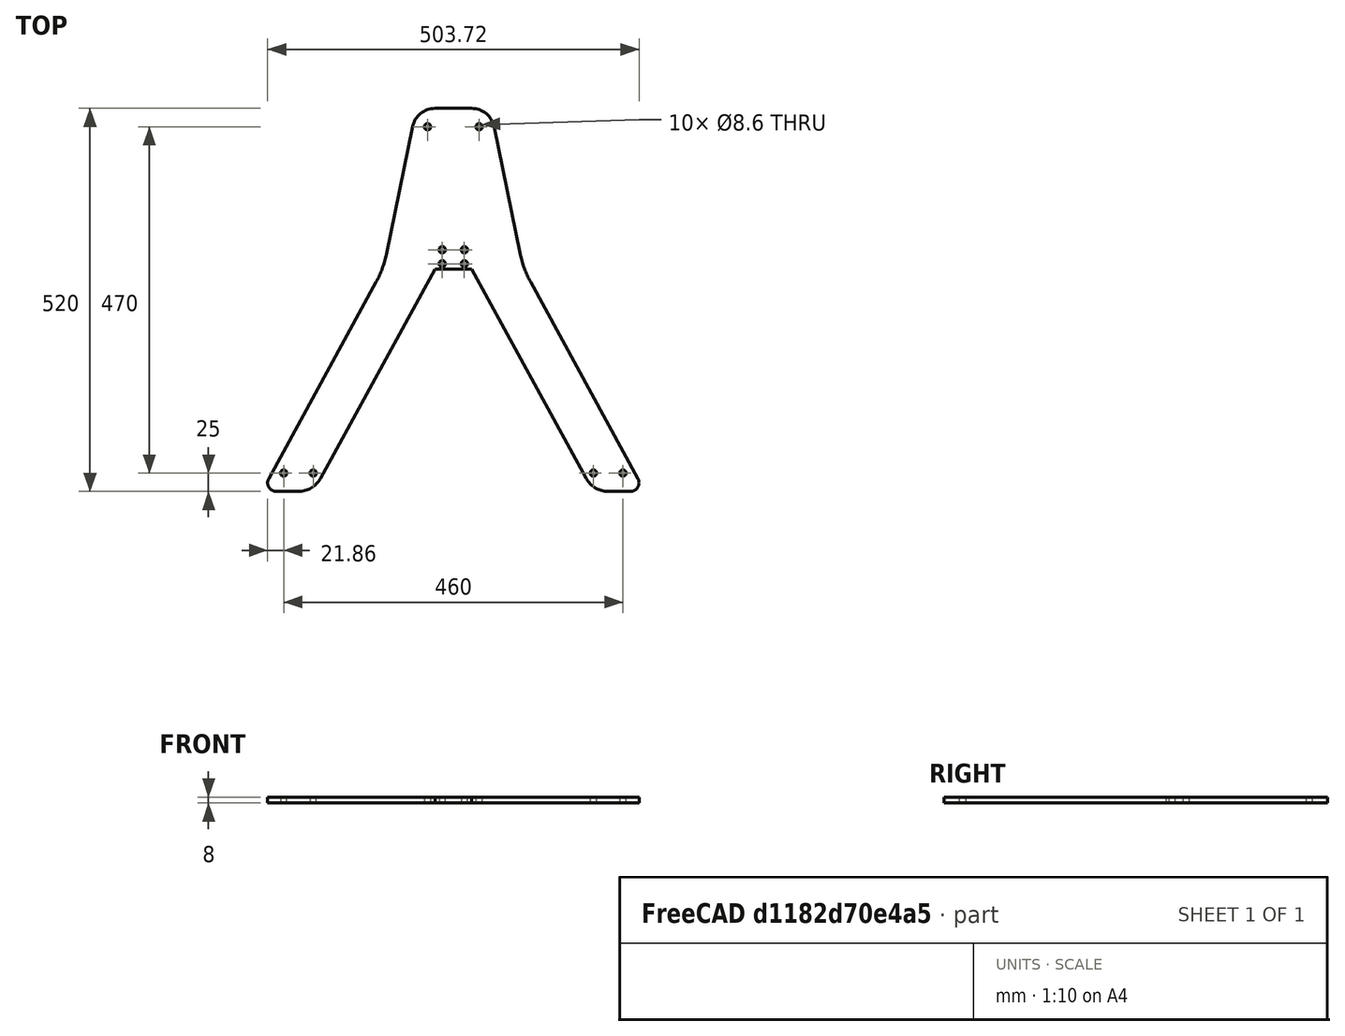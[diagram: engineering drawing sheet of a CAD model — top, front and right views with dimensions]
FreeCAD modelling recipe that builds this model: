
FCSTD DOCUMENT  (FreeCAD 0.17R12848 (Git))
Label: bienenwaage-unten
License: All rights reserved
LicenseURL: http://en.wikipedia.org/wiki/All_rights_reserved
objects: Sketcher::SketchObject×1, PartDesign::Pad×1, PartDesign::Body×1
note: 4 computed .brp shape members not serialized (recipe doc carries the construction recipe); baked Part::Feature solids carry a one-line shape summary decoded from their .brp

FEATURE [Sketcher::SketchObject] Sketch
  MapMode = 5
  Support = -> [XY_Plane]
  sketch-geometry (35):
    g0: Circle CenterX=245 CenterY=328 CenterZ=0 NormalX=0 NormalY=0 NormalZ=1 AngleXU=0 Radius=4.3
    g1: Circle CenterX=275 CenterY=328 CenterZ=0 NormalX=0 NormalY=0 NormalZ=1 AngleXU=0 Radius=4.3
    g2: Circle CenterX=275 CenterY=309 CenterZ=0 NormalX=0 NormalY=0 NormalZ=1 AngleXU=0 Radius=4.3
    g3: Circle CenterX=245 CenterY=309 CenterZ=0 NormalX=0 NormalY=0 NormalZ=1 AngleXU=0 Radius=4.3
    g4: LineSegment StartX=20 StartY=0 StartZ=0 EndX=50 EndY=0 EndZ=0
    g5: LineSegment StartX=79.5893 StartY=17.5512 StartZ=0 EndX=235 EndY=302 EndZ=0
    g6: LineSegment StartX=235 StartY=302 StartZ=0 EndX=285 EndY=302 EndZ=0
    g7: LineSegment StartX=285 StartY=302 StartZ=0 EndX=440.411 EndY=17.5512 EndZ=0
    g8: LineSegment StartX=470 StartY=0 StartZ=0 EndX=500 EndY=0 EndZ=0
    g9: LineSegment StartX=510.411 StartY=17.5512 StartZ=0 EndX=364.589 EndY=284.449 EndZ=0
    g10: LineSegment StartX=350.957 StartY=321.587 StartZ=0 EndX=315.054 EndY=495.516 EndZ=0
    g11: LineSegment StartX=204.946 StartY=495.516 StartZ=0 EndX=169.043 EndY=321.587 EndZ=0
    g12: LineSegment StartX=155.411 StartY=284.449 StartZ=0 EndX=9.58926 EndY=17.5512 EndZ=0
    g13: Circle CenterX=490 CenterY=25 CenterZ=0 NormalX=0 NormalY=0 NormalZ=1 AngleXU=0 Radius=4.3
    g14: Circle CenterX=450 CenterY=25 CenterZ=0 NormalX=0 NormalY=0 NormalZ=1 AngleXU=0 Radius=4.3
    g15: Circle CenterX=70 CenterY=25 CenterZ=0 NormalX=0 NormalY=0 NormalZ=1 AngleXU=0 Radius=4.3
    g16: Circle CenterX=30 CenterY=25 CenterZ=0 NormalX=0 NormalY=0 NormalZ=1 AngleXU=0 Radius=4.3
    g17: ArcOfCircle CenterX=500 CenterY=11.8633 CenterZ=0 NormalX=0 NormalY=0 NormalZ=1 AngleXU=0 Radius=11.8633 StartAngle=4.71239 EndAngle=6.78323
    g18: GeomPoint X=520 Y=0 Z=0
    g19: ArcOfCircle CenterX=20 CenterY=11.8633 CenterZ=0 NormalX=0 NormalY=0 NormalZ=1 AngleXU=0 Radius=11.8633 StartAngle=2.64155 EndAngle=4.71239
    g20: GeomPoint X=210 Y=520 Z=0
    g21: GeomPoint X=310 Y=520 Z=0
    g22: GeomPoint X=70 Y=0 Z=0
    g23: ArcOfCircle CenterX=50 CenterY=33.7176 CenterZ=0 NormalX=0 NormalY=0 NormalZ=1 AngleXU=0 Radius=33.7176 StartAngle=4.71239 EndAngle=5.78314
    g24: GeomPoint X=450 Y=0 Z=0
    g25: ArcOfCircle CenterX=470 CenterY=33.7176 CenterZ=0 NormalX=0 NormalY=0 NormalZ=1 AngleXU=0 Radius=33.7176 StartAngle=3.64164 EndAngle=4.71239
    g26: GeomPoint X=355 Y=302 Z=0
    g27: ArcOfCircle CenterX=482.118 CenterY=348.662 CenterZ=0 NormalX=0 NormalY=0 NormalZ=1 AngleXU=0 Radius=133.927 StartAngle=3.34516 EndAngle=3.64164
    g28: GeomPoint X=165 Y=302 Z=0
    g29: ArcOfCircle CenterX=37.8816 CenterY=348.662 CenterZ=0 NormalX=0 NormalY=0 NormalZ=1 AngleXU=0 Radius=133.927 StartAngle=5.78314 EndAngle=6.07962
    g30: LineSegment StartX=235 StartY=520 StartZ=0 EndX=285 EndY=520 EndZ=0
    g31: ArcOfCircle CenterX=235 CenterY=489.312 CenterZ=0 NormalX=0 NormalY=0 NormalZ=1 AngleXU=0 Radius=30.6876 StartAngle=1.5708 EndAngle=2.93803
    g32: ArcOfCircle CenterX=285 CenterY=489.312 CenterZ=0 NormalX=0 NormalY=0 NormalZ=1 AngleXU=0 Radius=30.6876 StartAngle=0.203563 EndAngle=1.5708
    g33: Circle CenterX=225 CenterY=495 CenterZ=0 NormalX=0 NormalY=0 NormalZ=1 AngleXU=0 Radius=4.3
    g34: Circle CenterX=295 CenterY=495 CenterZ=0 NormalX=0 NormalY=0 NormalZ=1 AngleXU=0 Radius=4.3
  constraints (90):
    c: DistanceY(g5,g3) = 7
    c: DistanceX(g5,g3) = 10
    c: DistanceX(g3,g2) = 30
    c: DistanceY(g2,g1) = 19
    c: Radius(g0) = 4.3
    c: Radius(g3) = 4.3
    c: Radius(g2) = 4.3
    c: Radius(g1) = 4.3
    c: Horizontal(g4)
    c: Coincident(g5,g6)
    c: Coincident(g6,g7)
    c: Horizontal(g8)
    c: DistanceX(g-1,g22) = 70
    c: DistanceX(g5,g28) = -70
    c: DistanceY(g5,g28) = 0
    c: DistanceX(g-1,g20) = 210
    c: DistanceX(g0,g3) = 0
    c: DistanceX(g1,g2) = 0
    c: DistanceY(g0,g1) = 0
    c: DistanceY(g6,g26) = 0
    c: DistanceY(g-1,g20) = 520
    c: DistanceX(g5,g6) = 50
    c: DistanceY(g-1,g5) = 302
    c: DistanceY(g3,g2) = 0
    c: DistanceY(g24,g22) = 0
    c: Horizontal(g6)
    c: DistanceX(g14,g24) = 0
    c: DistanceY(g24,g14) = 25
    c: DistanceY(g14,g13) = 0
    c: Radius(g13) = 4.3
    c: Radius(g14) = 4.3
    c: DistanceX(g16) = 30
    c: DistanceX(g15,g22) = 0
    c: DistanceY(g16,g15) = 0
    c: DistanceY(g-1,g16) = 25
    c: Radius(g16) = 4.3
    c: Radius(g15) = 4.3
    c: DistanceX(g6,g26) = 70
    c: Tangent(g8,g17) = -1.5708
    c: Tangent(g9,g17) = -1.5708
    c: DistanceX(g-1,g24) = 450
    c: Parallel(g7,g9)
    c: PointOnObject(g18,g-1)
    c: DistanceX(g-1,g18) = 520
    c: DistanceX(g8,g18) = 20
    c: DistanceX(g13,g18) = 30
    c: Parallel(g12,g5)
    c: Tangent(g12,g19) = -1.5708
    c: Tangent(g4,g19) = -1.5708
    c: DistanceX(g-1,g4) = 20
    c: DistanceY(g-1,g4) = 0
    c: Tangent(g4,g23) = -1.5708
    c: Tangent(g5,g23) = -1.5708
    c: DistanceY(g-1,g22) = 0
    c: Distance(g22,g4) = 20
    c: Distance(g22,g5) = 20
    c: Tangent(g8,g25) = -1.5708
    c: Tangent(g7,g25) = -1.5708
    c: DistanceY(g24,g8) = 0
    c: Distance(g24,g7) = 20
    c: Distance(g24,g8) = 20
    c: Tangent(g10,g27) = 1.5708
    c: Tangent(g9,g27) = 1.5708
    c: Distance(g26,g10) = 20
    c: Distance(g26,g9) = 20
    c: Tangent(g11,g29) = 1.5708
    c: Tangent(g12,g29) = 1.5708
    c: Distance(g28,g12) = 20
    c: Distance(g28,g11) = 20
    c: Distance(g-1,g12) = 20
    c: Distance(g9,g18) = 20
    c: DistanceX(g20,g21) = 100
    c: Horizontal(g11,g10)
    c: Tangent(g11,g31) = -1.5708
    c: Tangent(g30,g31) = 1.5708
    c: Tangent(g30,g32) = 1.5708
    c: Tangent(g10,g32) = -1.5708
    c: DistanceY(g21,g20) = 0
    c: Distance(g21,g10) = 25
    c: DistanceY(g30,g20) = 0
    c: Horizontal(g30,g30)
    c: Distance(g21,g30) = 25
    c: Distance(g20,g11) = 25
    c: Distance(g30,g20) = 25
    c: DistanceX(g20,g33) = 15
    c: DistanceX(g34,g21) = 15
    c: Horizontal(g33,g34)
    c: DistanceY(g33,g20) = 25
    c: Radius(g33) = 4.3
    c: Radius(g34) = 4.3
FEATURE [PartDesign::Pad] Pad
  Length = 8
  Length2 = 100
  Profile = -> Sketch
  Type = 0
FEATURE [PartDesign::Body] Body
  Group = -> [Sketch,Pad]
  Origin = -> Origin
  Tip = -> Pad
